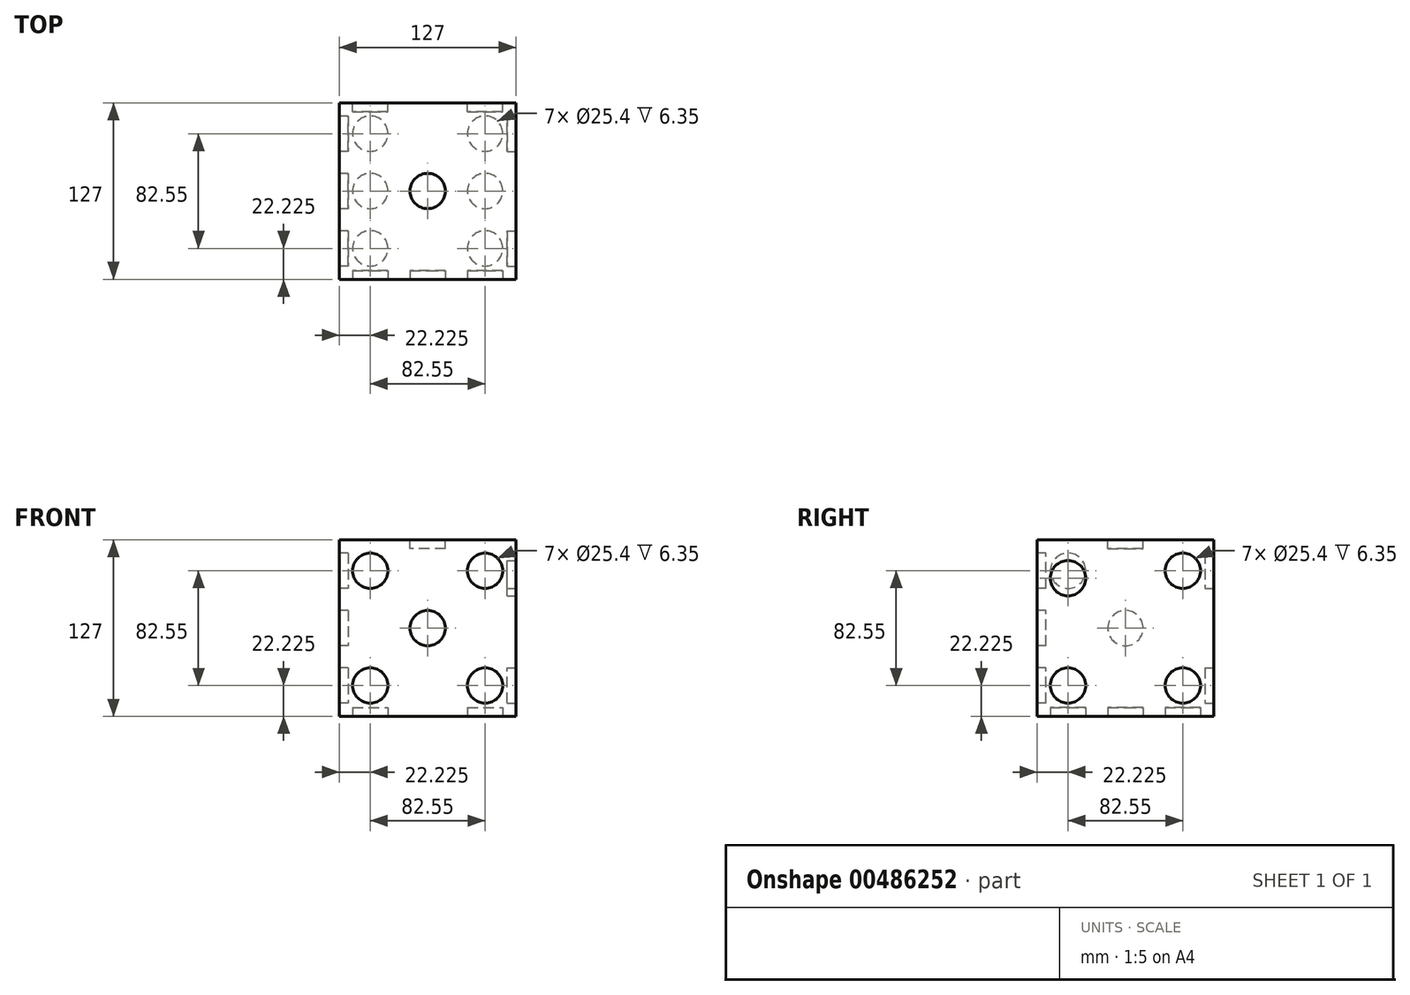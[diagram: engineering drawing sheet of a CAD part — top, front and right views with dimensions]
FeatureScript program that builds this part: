
annotation { "Feature Type Name" : "Feature", "Feature Type Description" : "" }
export const myFeature = defineFeature(function(context is Context, id is Id, definition is map)
    precondition{}
    {
        {
            var Q0;
            Q0=qCreatedBy(makeId("Top.planeOp"),FACE);
            var sketch = newSketch(context, id + "F0", { "sketchPlane" : qUnion([Q0])});
            skLineSegment(sketch, "E0.bottom", {"start": v(0, 0) * mm, "end": v(127, 0) * mm});
            skLineSegment(sketch, "E0.top", {"start": v(0, 127) * mm, "end": v(127, 127) * mm});
            skLineSegment(sketch, "E0.left", {"start": v(0, 0) * mm, "end": v(0, 127) * mm});
            skLineSegment(sketch, "E0.right", {"start": v(127, 0) * mm, "end": v(127, 127) * mm});
            skSolve(sketch);
        }
        {
            var Q0;
            Q0 = qSketchRegion(id + "F0", true);
            extrude(context, id + "F1", {"entities" : qUnion([Q0]), "depth" : 127 * mm});
        }
        {
            var Q0;
            Q0=makeQuery(id+"F1.opExtrude","CAP_FACE",FACE,{"disambiguationData":[OSD([sQuery(id+"F0.wireOp",EDGE,"E0.bottom"),sQuery(id+"F0.wireOp",EDGE,"E0.top"),sQuery(id+"F0.wireOp",EDGE,"E0.left"),sQuery(id+"F0.wireOp",EDGE,"E0.right")])],"isStart":false});
            var sketch = newSketch(context, id + "F2", { "sketchPlane" : qUnion([Q0])});
            skCircle(sketch, "E1", {"center": v(63.5, 63.5) * mm, "radius": 12.7 * mm});
            skPoint(sketch, "E1.centerSnap0", {"position": v(0, 63.5) * mm});
            skPoint(sketch, "E1.centerSnap1", {"position": v(63.5, 127) * mm});
            skSolve(sketch);
        }
        {
            var Q0;
            Q0=makeQuery(id+"F2.imprint","IMPRINT",FACE,{"disambiguationData":[TD([[makeQuery(id+"F2.imprint","IMPRINT",EDGE,{"derivedFrom":sQuery(id+"F2.wireOp",EDGE,"E1")}),1.0]])]});
            var Q1;
            Q1=sQuery(id+"F2.wireOp",EDGE,"E1");
            extrude(context, id + "F3", {"entities" : qUnion([Q0]), "operationType" : NewBodyOperationType.REMOVE, "surfaceEntities" : qUnion([Q1]), "oppositeDirection" : true, "depth" : 6.35 * mm});
        }
        {
            var Q0;
            Q0=makeQuery(id+"F1.opExtrude","SWEPT_FACE",FACE,{"disambiguationData":[OSD([sQuery(id+"F0.wireOp",EDGE,"E0.top")])]});
            var sketch = newSketch(context, id + "F4", { "sketchPlane" : qUnion([Q0])});
            skCircle(sketch, "E2", {"center": v(-104.78, 22.22) * mm, "radius": 12.7 * mm});
            skCircle(sketch, "E3", {"center": v(-22.23, 104.78) * mm, "radius": 12.7 * mm});
            skSolve(sketch);
        }
        {
            var Q0;
            Q0=makeQuery(id+"F4.imprint","IMPRINT",FACE,{"disambiguationData":[TD([[makeQuery(id+"F4.imprint","IMPRINT",EDGE,{"derivedFrom":sQuery(id+"F4.wireOp",EDGE,"E2")}),1.0]])]});
            var Q1;
            Q1=makeQuery(id+"F4.imprint","IMPRINT",FACE,{"disambiguationData":[TD([[makeQuery(id+"F4.imprint","IMPRINT",EDGE,{"derivedFrom":sQuery(id+"F4.wireOp",EDGE,"E3")}),1.0]])]});
            extrude(context, id + "F5", {"entities" : qUnion([Q0, Q1]), "operationType" : NewBodyOperationType.REMOVE, "oppositeDirection" : true, "depth" : 6.35 * mm});
        }
        {
            var Q0;
            Q0=makeQuery(id+"F1.opExtrude","SWEPT_FACE",FACE,{"disambiguationData":[OSD([sQuery(id+"F0.wireOp",EDGE,"E0.left")])]});
            var sketch = newSketch(context, id + "F6", { "sketchPlane" : qUnion([Q0])});
            skCircle(sketch, "E4", {"center": v(-104.78, 22.22) * mm, "radius": 12.7 * mm});
            skCircle(sketch, "E5", {"center": v(-63.5, 63.5) * mm, "radius": 12.7 * mm});
            skCircle(sketch, "E6", {"center": v(-22.23, 104.78) * mm, "radius": 12.7 * mm});
            skSolve(sketch);
        }
        {
            var Q0;
            Q0=makeQuery(id+"F6.imprint","IMPRINT",FACE,{"disambiguationData":[TD([[makeQuery(id+"F6.imprint","IMPRINT",EDGE,{"derivedFrom":sQuery(id+"F6.wireOp",EDGE,"E4")}),1.0]])]});
            var Q1;
            Q1=makeQuery(id+"F6.imprint","IMPRINT",FACE,{"disambiguationData":[TD([[makeQuery(id+"F6.imprint","IMPRINT",EDGE,{"derivedFrom":sQuery(id+"F6.wireOp",EDGE,"E5")}),1.0]])]});
            var Q2;
            Q2=makeQuery(id+"F6.imprint","IMPRINT",FACE,{"disambiguationData":[TD([[makeQuery(id+"F6.imprint","IMPRINT",EDGE,{"derivedFrom":sQuery(id+"F6.wireOp",EDGE,"E6")}),1.0]])]});
            extrude(context, id + "F7", {"entities" : qUnion([Q0, Q1, Q2]), "operationType" : NewBodyOperationType.REMOVE, "oppositeDirection" : true, "depth" : 6.35 * mm});
        }
        {
            var Q0;
            Q0=makeQuery(id+"F1.opExtrude","SWEPT_FACE",FACE,{"disambiguationData":[OSD([sQuery(id+"F0.wireOp",EDGE,"E0.right")])]});
            var sketch = newSketch(context, id + "F8", { "sketchPlane" : qUnion([Q0])});
            skCircle(sketch, "E7", {"center": v(22.23, 99.48) * mm, "radius": 12.7 * mm});
            skCircle(sketch, "E8", {"center": v(104.78, 104.78) * mm, "radius": 12.7 * mm});
            skCircle(sketch, "E9", {"center": v(104.78, 22.22) * mm, "radius": 12.7 * mm});
            skCircle(sketch, "E10", {"center": v(22.23, 22.22) * mm, "radius": 12.7 * mm});
            skSolve(sketch);
        }
        {
            var Q0;
            Q0=makeQuery(id+"F8.imprint","IMPRINT",FACE,{"disambiguationData":[TD([[makeQuery(id+"F8.imprint","IMPRINT",EDGE,{"derivedFrom":sQuery(id+"F8.wireOp",EDGE,"E7")}),1.0]])]});
            var Q1;
            Q1=makeQuery(id+"F8.imprint","IMPRINT",FACE,{"disambiguationData":[TD([[makeQuery(id+"F8.imprint","IMPRINT",EDGE,{"derivedFrom":sQuery(id+"F8.wireOp",EDGE,"E8")}),1.0]])]});
            var Q2;
            Q2=makeQuery(id+"F8.imprint","IMPRINT",FACE,{"disambiguationData":[TD([[makeQuery(id+"F8.imprint","IMPRINT",EDGE,{"derivedFrom":sQuery(id+"F8.wireOp",EDGE,"E9")}),1.0]])]});
            var Q3;
            Q3=makeQuery(id+"F8.imprint","IMPRINT",FACE,{"disambiguationData":[TD([[makeQuery(id+"F8.imprint","IMPRINT",EDGE,{"derivedFrom":sQuery(id+"F8.wireOp",EDGE,"E10")}),1.0]])]});
            extrude(context, id + "F9", {"entities" : qUnion([Q0, Q1, Q2, Q3]), "operationType" : NewBodyOperationType.REMOVE, "oppositeDirection" : true, "depth" : 6.35 * mm});
        }
        {
            var Q0;
            Q0=makeQuery(id+"F1.opExtrude","SWEPT_FACE",FACE,{"disambiguationData":[OSD([sQuery(id+"F0.wireOp",EDGE,"E0.bottom")])]});
            var sketch = newSketch(context, id + "F10", { "sketchPlane" : qUnion([Q0])});
            skCircle(sketch, "E11", {"center": v(22.23, 104.78) * mm, "radius": 12.7 * mm});
            skCircle(sketch, "E12", {"center": v(104.78, 104.78) * mm, "radius": 12.7 * mm});
            skCircle(sketch, "E13", {"center": v(63.5, 63.5) * mm, "radius": 12.7 * mm});
            skCircle(sketch, "E14", {"center": v(104.78, 22.22) * mm, "radius": 12.7 * mm});
            skCircle(sketch, "E15", {"center": v(22.23, 22.22) * mm, "radius": 12.7 * mm});
            skSolve(sketch);
        }
        {
            var Q0;
            Q0=makeQuery(id+"F10.imprint","IMPRINT",FACE,{"disambiguationData":[TD([[makeQuery(id+"F10.imprint","IMPRINT",EDGE,{"derivedFrom":sQuery(id+"F10.wireOp",EDGE,"E12")}),1.0]])]});
            var Q1;
            Q1=makeQuery(id+"F10.imprint","IMPRINT",FACE,{"disambiguationData":[TD([[makeQuery(id+"F10.imprint","IMPRINT",EDGE,{"derivedFrom":sQuery(id+"F10.wireOp",EDGE,"E14")}),1.0]])]});
            var Q2;
            Q2=makeQuery(id+"F10.imprint","IMPRINT",FACE,{"disambiguationData":[TD([[makeQuery(id+"F10.imprint","IMPRINT",EDGE,{"derivedFrom":sQuery(id+"F10.wireOp",EDGE,"E15")}),1.0]])]});
            var Q3;
            Q3=makeQuery(id+"F10.imprint","IMPRINT",FACE,{"disambiguationData":[TD([[makeQuery(id+"F10.imprint","IMPRINT",EDGE,{"derivedFrom":sQuery(id+"F10.wireOp",EDGE,"E13")}),1.0]])]});
            var Q4;
            Q4=makeQuery(id+"F10.imprint","IMPRINT",FACE,{"disambiguationData":[TD([[makeQuery(id+"F10.imprint","IMPRINT",EDGE,{"derivedFrom":sQuery(id+"F10.wireOp",EDGE,"E11")}),1.0]])]});
            extrude(context, id + "F11", {"entities" : qUnion([Q0, Q1, Q2, Q3, Q4]), "operationType" : NewBodyOperationType.REMOVE, "oppositeDirection" : true, "depth" : 6.35 * mm});
        }
        {
            var Q0;
            Q0=makeQuery(id+"F1.opExtrude","CAP_FACE",FACE,{"disambiguationData":[OSD([sQuery(id+"F0.wireOp",EDGE,"E0.bottom"),sQuery(id+"F0.wireOp",EDGE,"E0.top"),sQuery(id+"F0.wireOp",EDGE,"E0.left"),sQuery(id+"F0.wireOp",EDGE,"E0.right")])],"isStart":true});
            var sketch = newSketch(context, id + "F12", { "sketchPlane" : qUnion([Q0])});
            skCircle(sketch, "E16", {"center": v(22.23, -22.23) * mm, "radius": 12.7 * mm});
            skCircle(sketch, "E17", {"center": v(22.23, -63.5) * mm, "radius": 12.7 * mm});
            skCircle(sketch, "E18", {"center": v(22.23, -104.78) * mm, "radius": 12.7 * mm});
            skCircle(sketch, "E19", {"center": v(104.78, -22.23) * mm, "radius": 12.7 * mm});
            skCircle(sketch, "E20", {"center": v(104.78, -63.5) * mm, "radius": 12.7 * mm});
            skCircle(sketch, "E21", {"center": v(104.77, -104.78) * mm, "radius": 12.7 * mm});
            skSolve(sketch);
        }
        {
            var Q0;
            Q0 = qSketchRegion(id + "F12", true);
            extrude(context, id + "F13", {"entities" : qUnion([Q0]), "operationType" : NewBodyOperationType.REMOVE, "oppositeDirection" : true, "depth" : 6.35 * mm});
        }
    });
